# Revit family: Gira_537702
name_source: partatom
category: Electrical Fixtures
revit_build: Autodesk Revit 2017 (Build: 20160225_1515(x64)
units: mm (PartAtom-declared; Revit-internal decimal feet)

## family parameters
Cut with Voids When Loaded = No
Host = Face
Maintain Annotation Orientation = Yes
Part Type = Normal
Room Calculation Point = No
Round Connector Dimension = Use Diameter
Shared = No

## types (1)
- S3000 pres. + motion detec. 360° top BT Sentinel
    Available = No
    BIM (1) = https://media.stage.bim.site
    Bridging switch = No
    Category = Movement sensor complete
    Data sheet (1) = https://katalog.gira.de
    Default Elevation = 1219 mm
    Description = S3000 pr. mot.det.360° top BT Sent PW,System 3000 presence and motion detector 360 top unit BT,,pure white,Features:,- Automatic switching of lighting, depending on the movement of heat and ambient brightness.,- Operation with System 3000 switching or dimming insert or 3-wire auxiliary insert.,- Expansion of the detection range in combination with the 3-wire auxiliary insert.,- Operation with auxiliary insert, 2-wire, 3-wire or mechanical button.,- Covering panel to limit the detection range.,- Ceiling mounting on System 3000 flush-mounted insert.,Functions with the Gira Bluetooth app:,- Set the device as a presence detector or motion detector.,- Set the brightness threshold.,- Set the sensitivity of the three PIR sensors.,- Set the delay time.,- Override functions: Automatic mode, permanently on off, time-limited on off for 0.5 to 5 hours.,- Occupied-home simulation.,- Day mode.,- Walking test.,- Switch-off pre-warning.,With System 3000 switching insert:,- Short-term operation.,With System 3000 dimming insert:,- Constant light control.,- Switch on with the last brightness set, or a saved switch-on brightness.,- The switch-on brightness can only be saved permanently via the System 3000 auxiliary insert with operating top unit and the Gira Bluetooth app.
    Forced switch off = No
    Forced switch on = No
    GTIN = 4010337052227
    HAN = 537702
    HeinzeBIM = https://bimportal.heinze.de
    Manufacturer = Gira
    Manufacturer URL = https://www.gira.de
    Model = Presence detector
    Name = S3000 pres. + motion detec. 360° top BT Sentinel
    Remote operation = Yes
    Scan angle = 360
    Sensor type = Passive infrared
    Substation input = Yes
    Suitable for C-load = No
    Suitable for ceiling mounting = Yes
    Suitable for wall mounting = Yes
    Transparent = No
    URL = http://katalog.gira.de
    With DALI interface = No
    With alarm function = No
    With remote control = No
    With signal unit = No

## geometry (parser evidence)
native form markers: Blend x2, Sweep x3
no freeform markers — native parametric forms only
